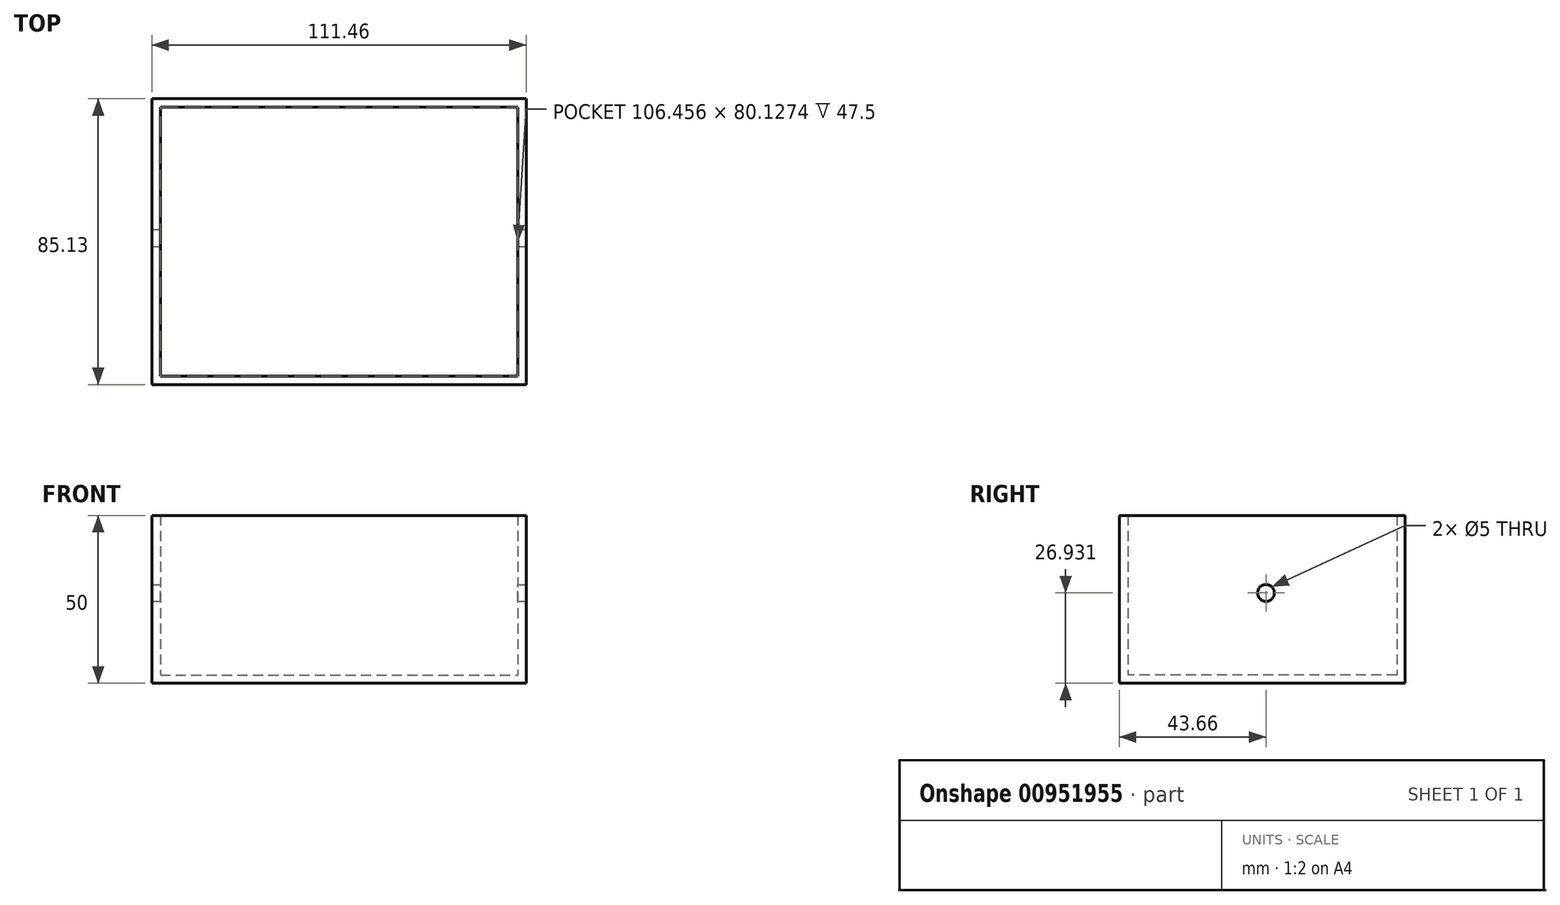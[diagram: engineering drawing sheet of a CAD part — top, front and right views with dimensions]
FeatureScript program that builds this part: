
annotation { "Feature Type Name" : "Feature", "Feature Type Description" : "" }
export const myFeature = defineFeature(function(context is Context, id is Id, definition is map)
    precondition{}
    {
        {
            var Q0;
            Q0=qCreatedBy(makeId("Top.planeOp"),FACE);
            var sketch = newSketch(context, id + "F0", { "sketchPlane" : qUnion([Q0])});
            skLineSegment(sketch, "E0.bottom", {"start": v(-51.56, 41.47) * mm, "end": v(59.9, 41.47) * mm});
            skLineSegment(sketch, "E0.top", {"start": v(-51.56, -43.66) * mm, "end": v(59.9, -43.66) * mm});
            skLineSegment(sketch, "E0.left", {"start": v(-51.56, 41.47) * mm, "end": v(-51.56, -43.66) * mm});
            skLineSegment(sketch, "E0.right", {"start": v(59.9, 41.47) * mm, "end": v(59.9, -43.66) * mm});
            skSolve(sketch);
        }
        {
            var Q0;
            Q0=makeQuery(id+"F0.imprint","IMPRINT",FACE,{"disambiguationData":[TD([[makeQuery(id+"F0.imprint","IMPRINT",EDGE,{"derivedFrom":sQuery(id+"F0.wireOp",EDGE,"E0.bottom")}),-1.0]])]});
            extrude(context, id + "F1", {"entities" : qUnion([Q0]), "depth" : 50 * mm, "offsetDistance" : 25 * mm});
        }
        {
            var Q0;
            Q0=makeQuery(id+"F1.opExtrude","CAP_FACE",FACE,{"disambiguationData":[OSD([sQuery(id+"F0.wireOp",EDGE,"E0.bottom"),sQuery(id+"F0.wireOp",EDGE,"E0.top"),sQuery(id+"F0.wireOp",EDGE,"E0.left"),sQuery(id+"F0.wireOp",EDGE,"E0.right")])],"isStart":false});
            shell(context, id + "F2", {"entities" : qUnion([Q0]), "thickness" : 2.5 * mm});
        }
        {
            var Q0;
            Q0=makeQuery(id+"F1.opExtrude","SWEPT_FACE",FACE,{"disambiguationData":[OSD([sQuery(id+"F0.wireOp",EDGE,"E0.right")])]});
            var sketch = newSketch(context, id + "F3", { "sketchPlane" : qUnion([Q0])});
            skCircle(sketch, "E1", {"center": v(0, 26.93) * mm, "radius": 9.4 * mm});
            skSolve(sketch);
        }
        {
            var Q0;
            Q0=sQuery(id+"F3.wireOp",VERTEX,"E1.center");
            var Q1;
            Q1=makeQuery(id+"F1.opExtrude","SWEPT_BODY",BODY,{"disambiguationData":[OSD([sQuery(id+"F0.wireOp",EDGE,"E0.bottom"),sQuery(id+"F0.wireOp",EDGE,"E0.top"),sQuery(id+"F0.wireOp",EDGE,"E0.left"),sQuery(id+"F0.wireOp",EDGE,"E0.right")])]});
            hole(context, id + "F4", {"style" : HoleStyle.SIMPLE, "endStyle" : HoleEndStyle.THROUGH, "holeDiameter" : 5 * mm, "majorDiameter" : 5 * mm, "isTappedThrough" : true, "tappedDepth" : 12 * mm, "tapClearance" : 3, "locations" : qUnion([Q0]), "scope" : qUnion([Q1])});
        }
    });
